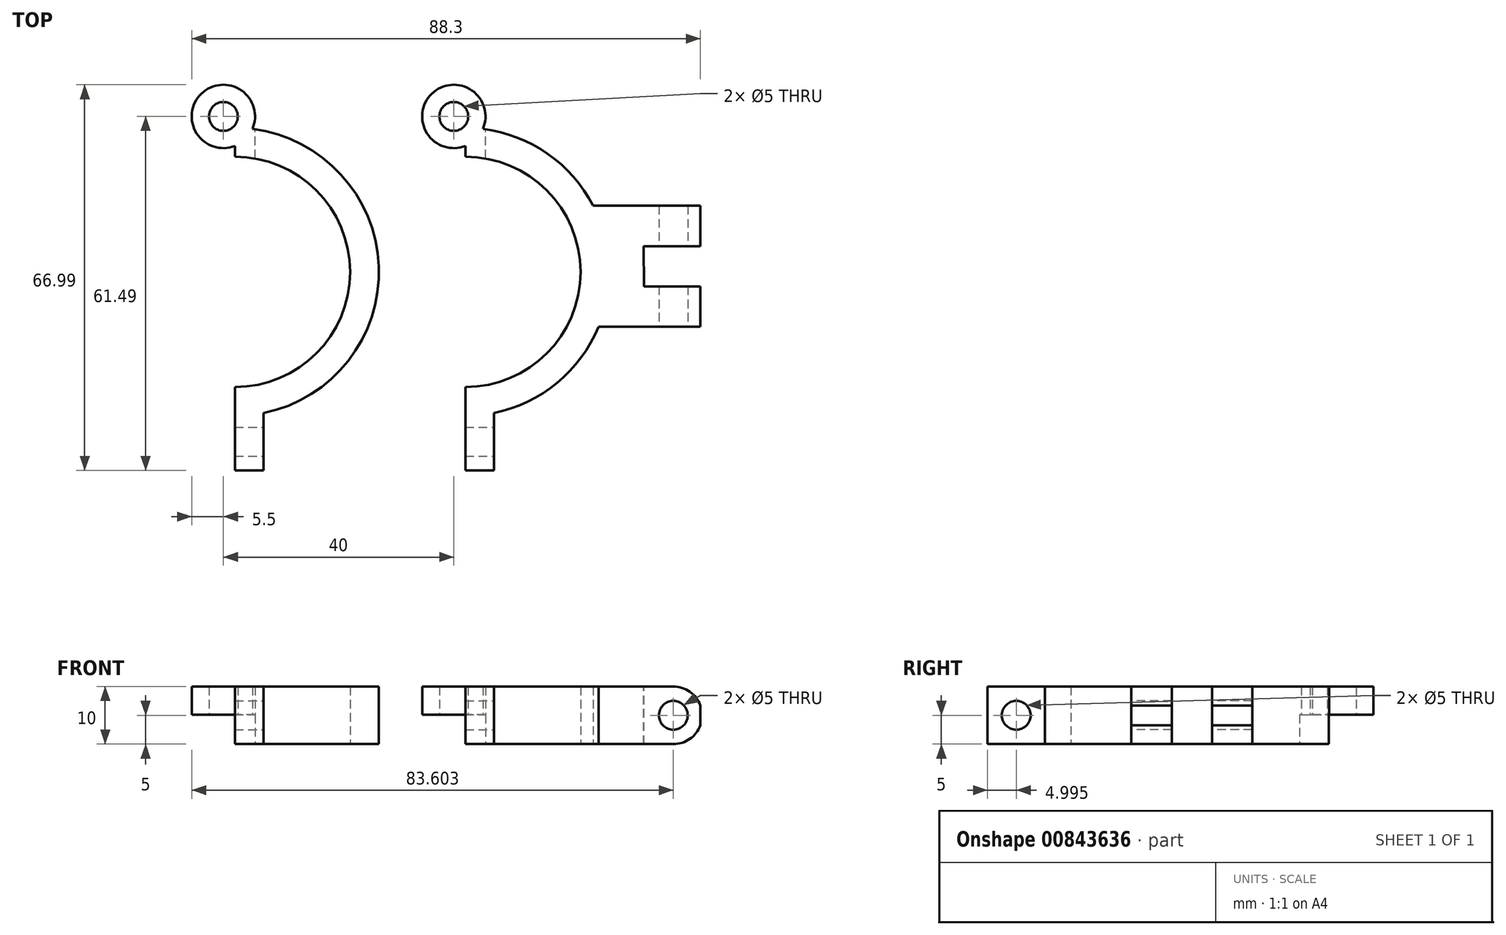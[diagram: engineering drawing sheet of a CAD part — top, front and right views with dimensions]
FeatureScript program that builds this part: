
annotation { "Feature Type Name" : "Feature", "Feature Type Description" : "" }
export const myFeature = defineFeature(function(context is Context, id is Id, definition is map)
    precondition{}
    {
        {
            var Q0;
            Q0=qCreatedBy(makeId("Top.planeOp"),FACE);
            var sketch = newSketch(context, id + "F0", { "sketchPlane" : qUnion([Q0])});
            skArc(sketch, "E0", {"start": v(0, -20) * mm, "mid": v(20, 0) * mm, "end": v(0, 20) * mm});
            skArc(sketch, "E1", {"start": v(5, -24.5) * mm, "mid": v(24.87, 2.51) * mm, "end": v(0, 25) * mm});
            skLineSegment(sketch, "E2", {"start": v(0, 25) * mm, "end": v(0, 20) * mm});
            skLineSegment(sketch, "E3.trimOffspring", {"start": v(0, -20) * mm, "end": v(0, -25) * mm});
            skLineSegment(sketch, "E4.top", {"start": v(0, -34.5) * mm, "end": v(5, -34.5) * mm});
            skLineSegment(sketch, "E4.left", {"start": v(0, -20) * mm, "end": v(0, -34.5) * mm});
            skLineSegment(sketch, "E4.right", {"start": v(5, -24.5) * mm, "end": v(5, -34.5) * mm});
            skLineSegment(sketch, "E5", {"start": v(0, 25) * mm, "end": v(-2, 25) * mm, "construction": true});
            skLineSegment(sketch, "E6", {"start": v(-2, 25) * mm, "end": v(-2, 27) * mm, "construction": true});
            skCircle(sketch, "E7", {"center": v(-2, 27) * mm, "radius": 2.5 * mm});
            skCircle(sketch, "E8", {"center": v(-2, 27) * mm, "radius": 5.5 * mm});
            skSolve(sketch);
        }
        {
            var Q0;
            Q0=qSketchRegion(id+"F0",true);
            extrude(context, id + "F1", {"entities" : qUnion([Q0]), "depth" : 10 * mm});
        }
        {
            var Q0;
            Q0=makeQuery(id+"F1.opExtrude","CAP_FACE",FACE,{"disambiguationData":[OSD([sQuery(id+"F0.wireOp",EDGE,"E0"),sQuery(id+"F0.wireOp",EDGE,"E1"),sQuery(id+"F0.wireOp",EDGE,"E2"),sQuery(id+"F0.wireOp",EDGE,"E4.top"),sQuery(id+"F0.wireOp",EDGE,"E4.left"),sQuery(id+"F0.wireOp",EDGE,"E4.right"),sQuery(id+"F0.wireOp",EDGE,"40993b52-42f4-45ce-a234-201135d0f319"),sQuery(id+"F0.wireOp",EDGE,"b42522cb-95ce-463a-b71a-0f81370b394c")])],"isStart":true});
            var sketch = newSketch(context, id + "F2", { "sketchPlane" : qUnion([Q0])});
            skArc(sketch, "E9.0", {"start": v(3.5, -27) * mm, "mid": v(-6.54, -30.1) * mm, "end": v(0, -21.88) * mm});
            skLineSegment(sketch, "E10.bottom", {"start": v(0, -15.05) * mm, "end": v(3.5, -15.05) * mm});
            skLineSegment(sketch, "E10.left", {"start": v(0, -15.05) * mm, "end": v(0, -21.88) * mm});
            skLineSegment(sketch, "E10.right", {"start": v(3.5, -15.05) * mm, "end": v(3.5, -27) * mm});
            skSolve(sketch);
        }
        {
            var Q0;
            Q0=qSketchRegion(id+"F2",true);
            extrude(context, id + "F3", {"entities" : qUnion([Q0]), "operationType" : NewBodyOperationType.REMOVE, "oppositeDirection" : true, "depth" : 5.1 * mm});
        }
        {
            var Q0;
            Q0=makeQuery(id+"F1.opExtrude","SWEPT_FACE",FACE,{"disambiguationData":[OSD([sQuery(id+"F0.wireOp",EDGE,"E4.right")])]});
            var sketch = newSketch(context, id + "F4", { "sketchPlane" : qUnion([Q0])});
            skLineSegment(sketch, "E11.0.0", {"start": v(-34.5, 0) * mm, "end": v(-24.5, 0) * mm, "construction": true});
            skLineSegment(sketch, "E11.0.1", {"start": v(-24.5, 0) * mm, "end": v(-24.5, 10) * mm, "construction": true});
            skLineSegment(sketch, "E11.0.2", {"start": v(-24.5, 10) * mm, "end": v(-34.5, 10) * mm, "construction": true});
            skLineSegment(sketch, "E11.0.3", {"start": v(-34.5, 10) * mm, "end": v(-34.5, 0) * mm, "construction": true});
            skCircle(sketch, "E12", {"center": v(-29.5, 5) * mm, "radius": 2.5 * mm});
            skPoint(sketch, "E12.centerSnap0", {"position": v(-29.5, 10) * mm});
            skPoint(sketch, "E12.centerSnap1", {"position": v(-34.5, 5) * mm});
            skSolve(sketch);
        }
        {
            var Q0;
            Q0=qSketchRegion(id+"F4",true);
            extrude(context, id + "F5", {"entities" : qUnion([Q0]), "operationType" : NewBodyOperationType.REMOVE, "oppositeDirection" : true, "depth" : 25 * mm});
        }
        {
            var Q0;
            Q0=makeQuery(id+"F1.opExtrude","SWEPT_BODY",BODY,{"disambiguationData":[OSD([sQuery(id+"F0.wireOp",EDGE,"E0"),sQuery(id+"F0.wireOp",EDGE,"E1"),sQuery(id+"F0.wireOp",EDGE,"E2"),sQuery(id+"F0.wireOp",EDGE,"E4.top"),sQuery(id+"F0.wireOp",EDGE,"E4.left"),sQuery(id+"F0.wireOp",EDGE,"E4.right"),sQuery(id+"F0.wireOp",EDGE,"E7"),sQuery(id+"F0.wireOp",EDGE,"E8")])]});
            transform(context, id + "F6", {"entities" : qUnion([Q0]), "transformType" : TransformType.TRANSLATION_3D, "dx" : 40 * mm, "dy" : 0 * mm, "dz" : 0 * mm, "makeCopy" : true});
        }
        {
            var Q0;
            Q0=makeQuery(id+"F6.opPattern","COPY",FACE,{"derivedFrom":makeQuery(id+"F1.opExtrude","CAP_FACE",FACE,{"disambiguationData":[OSD([sQuery(id+"F0.wireOp",EDGE,"E0"),sQuery(id+"F0.wireOp",EDGE,"E1"),sQuery(id+"F0.wireOp",EDGE,"E2"),sQuery(id+"F0.wireOp",EDGE,"E4.top"),sQuery(id+"F0.wireOp",EDGE,"E4.left"),sQuery(id+"F0.wireOp",EDGE,"E4.right"),sQuery(id+"F0.wireOp",EDGE,"E7"),sQuery(id+"F0.wireOp",EDGE,"E8")])],"isStart":false}),"instanceName":"1"});
            var sketch = newSketch(context, id + "F7", { "sketchPlane" : qUnion([Q0])});
            skLineSegment(sketch, "E13.rect.bottom", {"start": v(61.08, -9.51) * mm, "end": v(81.1, -9.51) * mm});
            skLineSegment(sketch, "E13.rect.top", {"start": v(60.88, 11.49) * mm, "end": v(80.89, 11.49) * mm});
            skPoint(sketch, "E13.rect.middle", {"position": v(64.98, 0.99) * mm});
            skLineSegment(sketch, "E14.0", {"start": v(61.08, -9.51) * mm, "end": v(60.88, 11.49) * mm});
            skLineSegment(sketch, "E15.0", {"start": v(60.88, 4.49) * mm, "end": v(60.95, 4.49) * mm});
            skLineSegment(sketch, "E16.0", {"start": v(60.88, -2.51) * mm, "end": v(61.01, -2.51) * mm});
            skLineSegment(sketch, "E17.0", {"start": v(71.08, -9.6) * mm, "end": v(71.08, -9.51) * mm});
            skLineSegment(sketch, "E18.trimOffspring", {"start": v(70.95, 4.49) * mm, "end": v(80.89, 4.49) * mm});
            skLineSegment(sketch, "E19.trimOffspring", {"start": v(71.01, -2.51) * mm, "end": v(81.01, -2.51) * mm});
            skLineSegment(sketch, "E20.trimOffspring", {"start": v(71.01, -2.51) * mm, "end": v(70.95, 4.49) * mm});
            skLineSegment(sketch, "E21", {"start": v(80.89, 11.49) * mm, "end": v(80.89, 4.49) * mm});
            skLineSegment(sketch, "E22", {"start": v(81.01, -2.51) * mm, "end": v(81.1, -9.51) * mm});
            skSolve(sketch);
        }
        {
            var Q0;
            Q0=qSketchRegion(id+"F7",true);
            extrude(context, id + "F8", {"entities" : qUnion([Q0]), "operationType" : NewBodyOperationType.ADD, "oppositeDirection" : true, "depth" : 10 * mm});
        }
        {
            var Q0;
            Q0=makeQuery(id+"F8.opExtrude","SWEPT_FACE",FACE,{"disambiguationData":[OSD([sQuery(id+"F7.wireOp",EDGE,"E13.rect.bottom")])]});
            var sketch = newSketch(context, id + "F9", { "sketchPlane" : qUnion([Q0])});
            skLineSegment(sketch, "E23.0", {"start": v(71.1, 0) * mm, "end": v(71.1, 10) * mm});
            skLineSegment(sketch, "E24.0.1", {"start": v(71.1, 0) * mm, "end": v(81.1, 0) * mm});
            skLineSegment(sketch, "E24.0.2", {"start": v(81.1, 0) * mm, "end": v(81.1, 10) * mm});
            skLineSegment(sketch, "E24.0.3", {"start": v(81.1, 10) * mm, "end": v(71.1, 10) * mm});
            skCircle(sketch, "E25", {"center": v(76.1, 5) * mm, "radius": 2.5 * mm});
            skPoint(sketch, "E25.centerSnap0", {"position": v(81.1, 5) * mm});
            skPoint(sketch, "E25.centerSnap1", {"position": v(76.1, 10) * mm});
            skSolve(sketch);
        }
        {
            var Q0;
            Q0=makeQuery(id+"F9.imprint","IMPRINT",FACE,{"disambiguationData":[TD([[makeQuery(id+"F9.imprint","IMPRINT",EDGE,{"derivedFrom":sQuery(id+"F9.wireOp",EDGE,"E25")}),1.0]])]});
            extrude(context, id + "F10", {"entities" : qUnion([Q0]), "operationType" : NewBodyOperationType.REMOVE, "oppositeDirection" : true, "depth" : 25 * mm});
        }
        {
            var Q0;
            Q0=makeQuery(id+"F8.opExtrude","SWEPT_FACE",FACE,{"disambiguationData":[OSD([sQuery(id+"F7.wireOp",EDGE,"E13.rect.bottom")])]});
            var sketch = newSketch(context, id + "F11", { "sketchPlane" : qUnion([Q0])});
            skArc(sketch, "E26", {"start": v(76.1, 0) * mm, "mid": v(81.1, 5) * mm, "end": v(76.1, 10) * mm});
            skLineSegment(sketch, "E27.bottom", {"start": v(81.1, 10) * mm, "end": v(76.1, 10) * mm});
            skLineSegment(sketch, "E27.top", {"start": v(80.98, 0) * mm, "end": v(76.1, 0) * mm});
            skLineSegment(sketch, "E28.0", {"start": v(80.8, 0) * mm, "end": v(80.8, 10) * mm});
            skSolve(sketch);
        }
        {
            var Q0;
            {var subQ3=sQuery(id+"F11.wireOp",EDGE,"E27.bottom");Q0=makeQuery(id+"F11.imprint","IMPRINT",FACE,{"disambiguationData":[TD([[makeQuery(id+"F11.imprint","IMPRINT",EDGE,{"derivedFrom":subQ3}),-1.0]])]});}
            var Q1;
            {var subQ3=sQuery(id+"F11.wireOp",EDGE,"E27.top");Q1=makeQuery(id+"F11.imprint","IMPRINT",FACE,{"disambiguationData":[TD([[makeQuery(id+"F11.imprint","IMPRINT",EDGE,{"derivedFrom":subQ3}),1.0]])]});}
            var Q2;
            {var subQ3=sQuery(id+"F11.wireOp",EDGE,"E27.top");var subQ5=sQuery(id+"F11.wireOp",EDGE,"E28.0");var subQ7=makeQuery(id+"F11.imprint","INTERSECT",VERTEX,{"derivedFrom":[subQ3,subQ5]});Q2=makeQuery(id+"F11.imprint","IMPRINT",FACE,{"disambiguationData":[TD([[makeQuery(id+"F11.imprint","IMPRINT",EDGE,{"disambiguationData":[TD([[subQ7,-1.0]])],"derivedFrom":subQ5}),-1.0]])]});}
            var Q3;
            {var subQ3=sQuery(id+"F11.wireOp",EDGE,"E27.bottom");var subQ5=sQuery(id+"F11.wireOp",EDGE,"E28.0");var subQ7=makeQuery(id+"F11.imprint","INTERSECT",VERTEX,{"derivedFrom":[subQ3,subQ5]});Q3=makeQuery(id+"F11.imprint","IMPRINT",FACE,{"disambiguationData":[TD([[makeQuery(id+"F11.imprint","IMPRINT",EDGE,{"disambiguationData":[TD([[subQ7,1.0]])],"derivedFrom":subQ5}),-1.0]])]});}
            var Q4;
            {var subQ0=sQuery(id+"F11.wireOp",EDGE,"E28.0");var subQ1=sQuery(id+"F11.wireOp",EDGE,"E26");var subQ3=makeQuery(id+"F11.imprint","INTERSECT",VERTEX,{"disambiguationData":[OD(0.0)],"derivedFrom":[subQ1,subQ0]});Q4=makeQuery(id+"F11.imprint","IMPRINT",FACE,{"disambiguationData":[TD([[makeQuery(id+"F11.imprint","IMPRINT",EDGE,{"disambiguationData":[TD([[subQ3,-1.0]])],"derivedFrom":subQ0}),-1.0]])]});}
            extrude(context, id + "F12", {"entities" : qUnion([Q0, Q1, Q2, Q3, Q4]), "operationType" : NewBodyOperationType.REMOVE, "oppositeDirection" : true, "depth" : 25 * mm});
        }
    });
